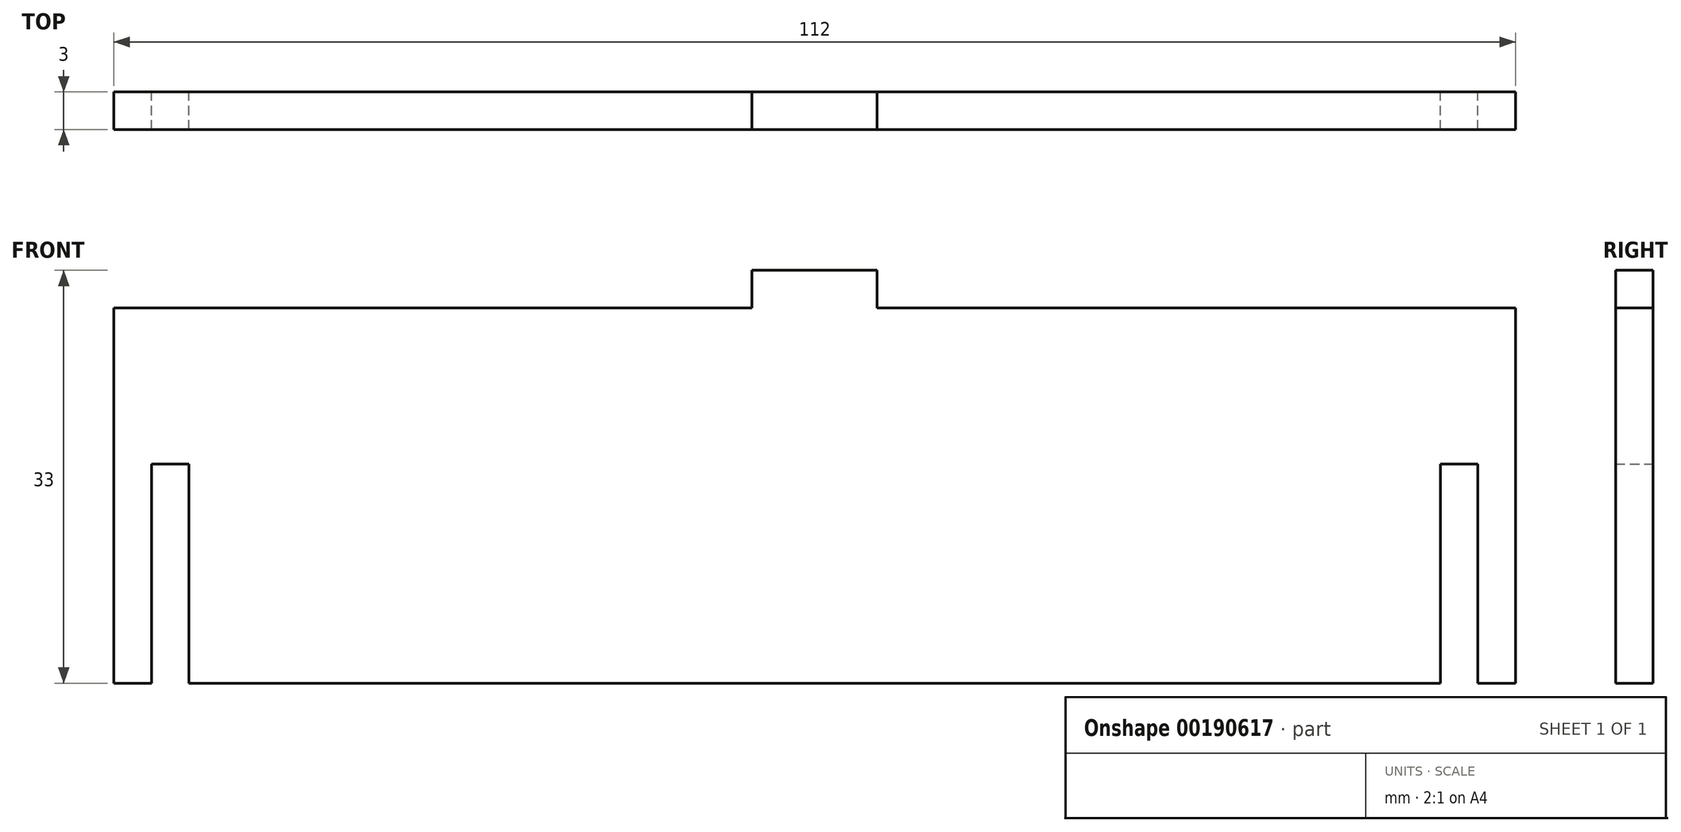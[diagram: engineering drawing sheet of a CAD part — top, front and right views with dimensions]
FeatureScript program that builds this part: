
annotation { "Feature Type Name" : "Feature", "Feature Type Description" : "" }
export const myFeature = defineFeature(function(context is Context, id is Id, definition is map)
    precondition{}
    {
        {
            var Q0;
            Q0=qCreatedBy(makeId("Front.planeOp"),FACE);
            var sketch = newSketch(context, id + "F0", { "sketchPlane" : qUnion([Q0])});
            skLineSegment(sketch, "E0.bottom", {"start": v(56, 15) * mm, "end": v(5, 15) * mm});
            skLineSegment(sketch, "E0.top", {"start": v(56, -15) * mm, "end": v(53, -15) * mm});
            skLineSegment(sketch, "E0.left", {"start": v(56, 15) * mm, "end": v(56, -15) * mm});
            skLineSegment(sketch, "E0.right", {"start": v(-56, 15) * mm, "end": v(-56, -15) * mm});
            skPoint(sketch, "E0.middle", {"position": v(0, 0) * mm});
            skLineSegment(sketch, "E1", {"start": v(-53, -15) * mm, "end": v(-53, 2.5) * mm});
            skLineSegment(sketch, "E2", {"start": v(-53, 2.5) * mm, "end": v(-50, 2.5) * mm});
            skLineSegment(sketch, "E3", {"start": v(-50, 2.5) * mm, "end": v(-50, -15) * mm});
            skLineSegment(sketch, "E4", {"start": v(50, -15) * mm, "end": v(50, 2.5) * mm});
            skLineSegment(sketch, "E5", {"start": v(50, 2.5) * mm, "end": v(53, 2.5) * mm});
            skLineSegment(sketch, "E6", {"start": v(53, 2.5) * mm, "end": v(53, -15) * mm});
            skLineSegment(sketch, "E7", {"start": v(-53, -15) * mm, "end": v(-56, -15) * mm});
            skLineSegment(sketch, "E8", {"start": v(50, -15) * mm, "end": v(-50, -15) * mm});
            skLineSegment(sketch, "E9", {"start": v(-5, 15) * mm, "end": v(-5, 18) * mm});
            skLineSegment(sketch, "E10", {"start": v(-5, 18) * mm, "end": v(5, 18) * mm});
            skLineSegment(sketch, "E11", {"start": v(5, 18) * mm, "end": v(5, 15) * mm});
            skLineSegment(sketch, "E12", {"start": v(-5, 15) * mm, "end": v(-56, 15) * mm});
            skLineSegment(sketch, "E13", {"start": v(0, 18) * mm, "end": v(0, 0) * mm, "construction": true});
            skSolve(sketch);
        }
        {
            var Q0;
            Q0=makeQuery(id+"F0.imprint","IMPRINT",FACE,{"disambiguationData":[TD([[makeQuery(id+"F0.imprint","IMPRINT",EDGE,{"derivedFrom":sQuery(id+"F0.wireOp",EDGE,"E0.bottom")}),1.0]])]});
            extrude(context, id + "F1", {"entities" : qUnion([Q0]), "depth" : 3 * mm});
        }
    });
